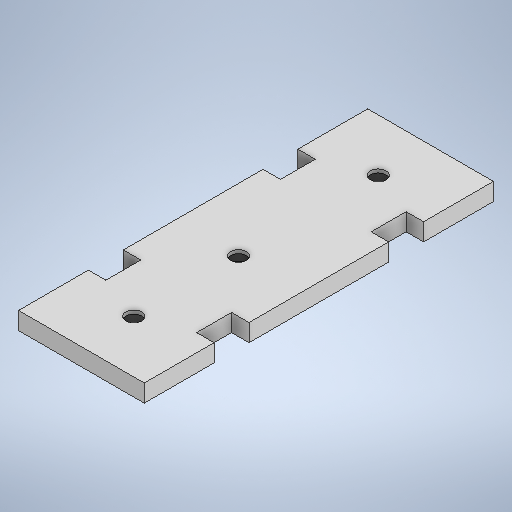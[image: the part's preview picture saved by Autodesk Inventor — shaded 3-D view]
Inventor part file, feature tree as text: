
AUTODESK INVENTOR PART (.ipt)
format: ipt  version: 2025.2 (Build 292293000, 293)  size: 268,288 bytes
history: native  units: mm
features: extrude x2, sketch x2
ambient origin geometry x8: Origin, YZ Plane, XZ Plane, XY Plane, X Axis, Y Axis, Z Axis, Center Point
bodies: Solid1 (feature_tree)
feature tree (4):
  extrude  "Extrusion1"  Depth=100.0mm
  extrude  "Extrusion2"  Depth=20.0mm
  sketch  "Sketch2"  dims[d0=36.0mm d1=100.0mm]
  sketch  "Sketch3"  dims[d2=20.0mm d3=20.0mm d4=10.0mm d5=5.0mm d6=10.0mm d7=5.0mm d8=5.0mm d9=15.0mm d11=30.0mm d12=10.1mm d13=40.0mm d14=10.1mm d15=5.0mm d16=0.0mm d18=4.5mm d19=4.5mm d20=4.5mm d21=1.0mm d22=0.0mm]
